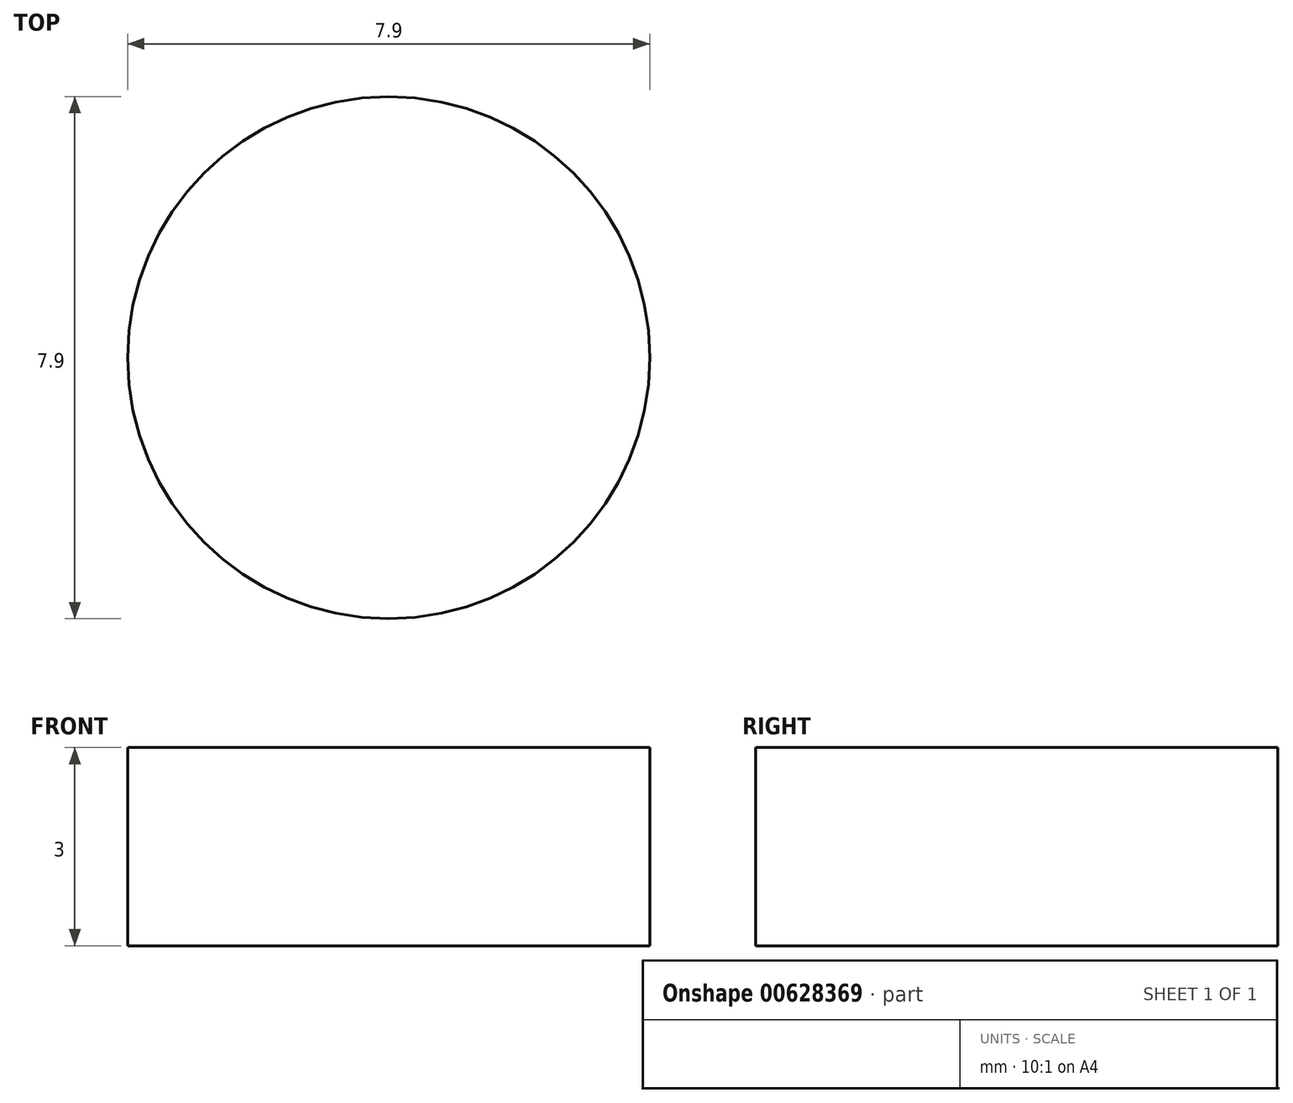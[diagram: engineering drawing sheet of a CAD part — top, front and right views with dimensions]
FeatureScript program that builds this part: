
annotation { "Feature Type Name" : "Feature", "Feature Type Description" : "" }
export const myFeature = defineFeature(function(context is Context, id is Id, definition is map)
    precondition{}
    {
        {
            var Q0;
            Q0=qCreatedBy(makeId("Top.planeOp"),FACE);
            var sketch = newSketch(context, id + "F0", { "sketchPlane" : qUnion([Q0])});
            skCircle(sketch, "E0", {"center": v(0, 0) * mm, "radius": 3.95 * mm});
            skSolve(sketch);
        }
        {
            var Q0;
            Q0 = qSketchRegion(id + "F0", true);
            extrude(context, id + "F1", {"entities" : qUnion([Q0]), "depth" : 3 * mm, "offsetDistance" : 25 * mm});
        }
    });
